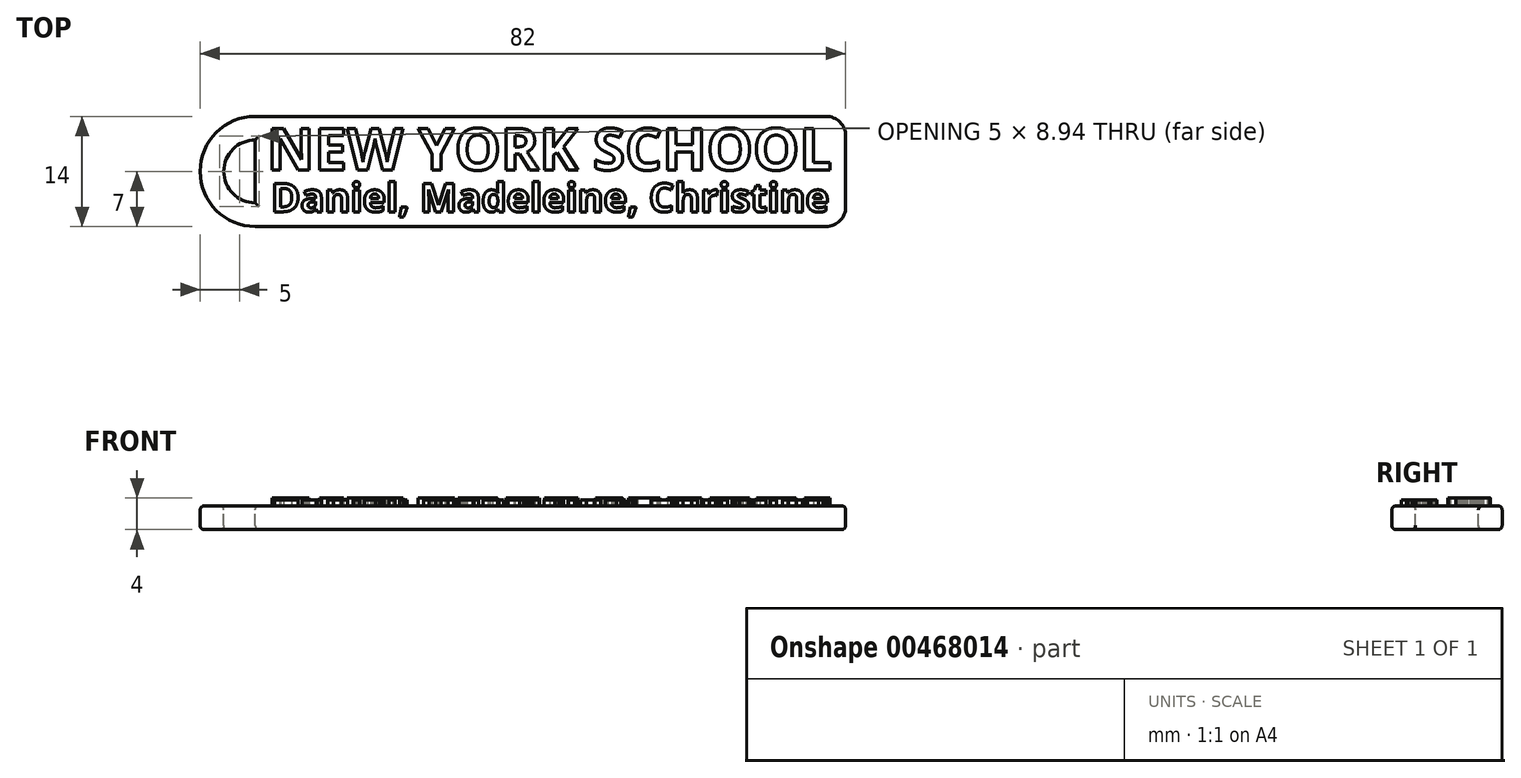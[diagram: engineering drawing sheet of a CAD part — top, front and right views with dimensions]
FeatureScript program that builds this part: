
annotation { "Feature Type Name" : "Feature", "Feature Type Description" : "" }
export const myFeature = defineFeature(function(context is Context, id is Id, definition is map)
    precondition{}
    {
        {
            var Q0;
            Q0=qCreatedBy(makeId("Top.planeOp"),FACE);
            var sketch = newSketch(context, id + "F0", { "sketchPlane" : qUnion([Q0])});
            skLineSegment(sketch, "E0.bottom", {"start": v(37.5, -7) * mm, "end": v(-37.5, -7) * mm});
            skLineSegment(sketch, "E0.top", {"start": v(37.5, 7) * mm, "end": v(-37.5, 7) * mm});
            skLineSegment(sketch, "E0.left", {"start": v(37.5, -7) * mm, "end": v(37.5, 7) * mm});
            skLineSegment(sketch, "E0.right", {"start": v(-37.5, -7) * mm, "end": v(-37.5, 7) * mm});
            skPoint(sketch, "E0.middle", {"position": v(0, 0) * mm});
            skSolve(sketch);
        }
        {
            var Q0;
            Q0=makeQuery(id+"F0.imprint","IMPRINT",FACE,{"disambiguationData":[TD([[makeQuery(id+"F0.imprint","IMPRINT",EDGE,{"derivedFrom":sQuery(id+"F0.wireOp",EDGE,"E0.bottom")}),-1.0]])]});
            extrude(context, id + "F1", {"entities" : qUnion([Q0]), "depth" : 3 * mm, "offsetDistance" : 25 * mm});
        }
        {
            var Q0;
            Q0=makeQuery(id+"F1.opExtrude","CAP_FACE",FACE,{"disambiguationData":[OSD([sQuery(id+"F0.wireOp",EDGE,"E0.bottom"),sQuery(id+"F0.wireOp",EDGE,"E0.top"),sQuery(id+"F0.wireOp",EDGE,"E0.left"),sQuery(id+"F0.wireOp",EDGE,"E0.right")])],"isStart":false});
            var sketch = newSketch(context, id + "F2", { "sketchPlane" : qUnion([Q0])});
            skText(sketch, "E1", { "text": "NEW YORK SCHOOL", "fontName": "OpenSans-Bold.ttf"});
            const initialGuessF2  = {"E1": [-0.036, 0.00018, 1, 0, 0.00532]};
            skSetInitialGuess(sketch, initialGuessF2);
            skSolve(sketch);
        }
        {
            var Q0;
            Q0=makeQuery(id+"F2.imprint","IMPRINT",FACE,{"disambiguationData":[TD([[makeQuery(id+"F2.imprint","IMPRINT",EDGE,{"derivedFrom":sQuery(id+"F2.wireOp",EDGE,"E1.sketch_text.stroke-0")}),-1.0]])]});
            var Q1;
            Q1=makeQuery(id+"F2.imprint","IMPRINT",FACE,{"disambiguationData":[TD([[makeQuery(id+"F2.imprint","IMPRINT",EDGE,{"derivedFrom":sQuery(id+"F2.wireOp",EDGE,"E1.sketch_text.stroke-14")}),-1.0]])]});
            var Q2;
            Q2=makeQuery(id+"F2.imprint","IMPRINT",FACE,{"disambiguationData":[TD([[makeQuery(id+"F2.imprint","IMPRINT",EDGE,{"derivedFrom":sQuery(id+"F2.wireOp",EDGE,"E1.sketch_text.stroke-26")}),-1.0]])]});
            var Q3;
            Q3=makeQuery(id+"F2.imprint","IMPRINT",FACE,{"disambiguationData":[TD([[makeQuery(id+"F2.imprint","IMPRINT",EDGE,{"derivedFrom":sQuery(id+"F2.wireOp",EDGE,"E1.sketch_text.stroke-50")}),-1.0]])]});
            var Q4;
            Q4=makeQuery(id+"F2.imprint","IMPRINT",FACE,{"disambiguationData":[TD([[makeQuery(id+"F2.imprint","IMPRINT",EDGE,{"derivedFrom":sQuery(id+"F2.wireOp",EDGE,"E1.sketch_text.stroke-59")}),-1.0]])]});
            var Q5;
            Q5=makeQuery(id+"F2.imprint","IMPRINT",FACE,{"disambiguationData":[TD([[makeQuery(id+"F2.imprint","IMPRINT",EDGE,{"derivedFrom":sQuery(id+"F2.wireOp",EDGE,"E1.sketch_text.stroke-73")}),-1.0]])]});
            var Q6;
            Q6=makeQuery(id+"F2.imprint","IMPRINT",FACE,{"disambiguationData":[TD([[makeQuery(id+"F2.imprint","IMPRINT",EDGE,{"derivedFrom":sQuery(id+"F2.wireOp",EDGE,"E1.sketch_text.stroke-92")}),-1.0]])]});
            var Q7;
            Q7=makeQuery(id+"F2.imprint","IMPRINT",FACE,{"disambiguationData":[TD([[makeQuery(id+"F2.imprint","IMPRINT",EDGE,{"derivedFrom":sQuery(id+"F2.wireOp",EDGE,"E1.sketch_text.stroke-105")}),-1.0]])]});
            var Q8;
            Q8=makeQuery(id+"F2.imprint","IMPRINT",FACE,{"disambiguationData":[TD([[makeQuery(id+"F2.imprint","IMPRINT",EDGE,{"derivedFrom":sQuery(id+"F2.wireOp",EDGE,"E1.sketch_text.stroke-133")}),-1.0]])]});
            var Q9;
            Q9=makeQuery(id+"F2.imprint","IMPRINT",FACE,{"disambiguationData":[TD([[makeQuery(id+"F2.imprint","IMPRINT",EDGE,{"derivedFrom":sQuery(id+"F2.wireOp",EDGE,"E1.sketch_text.stroke-148")}),-1.0]])]});
            var Q10;
            Q10=makeQuery(id+"F2.imprint","IMPRINT",FACE,{"disambiguationData":[TD([[makeQuery(id+"F2.imprint","IMPRINT",EDGE,{"derivedFrom":sQuery(id+"F2.wireOp",EDGE,"E1.sketch_text.stroke-160")}),-1.0]])]});
            var Q11;
            Q11=makeQuery(id+"F2.imprint","IMPRINT",FACE,{"disambiguationData":[TD([[makeQuery(id+"F2.imprint","IMPRINT",EDGE,{"derivedFrom":sQuery(id+"F2.wireOp",EDGE,"E1.sketch_text.stroke-174")}),-1.0]])]});
            var Q12;
            Q12=makeQuery(id+"F2.imprint","IMPRINT",FACE,{"disambiguationData":[TD([[makeQuery(id+"F2.imprint","IMPRINT",EDGE,{"derivedFrom":sQuery(id+"F2.wireOp",EDGE,"E1.sketch_text.stroke-188")}),-1.0]])]});
            extrude(context, id + "F3", {"entities" : qUnion([Q0, Q1, Q2, Q3, Q4, Q5, Q6, Q7, Q8, Q9, Q10, Q11, Q12]), "operationType" : NewBodyOperationType.ADD, "depth" : 1 * mm, "offsetDistance" : 25 * mm});
        }
        {
            var Q0;
            {var subQ0=sQuery(id+"F0.wireOp",EDGE,"E0.top");var subQ1=sQuery(id+"F0.wireOp",EDGE,"E0.right");var subQ2=sQuery(id+"F0.wireOp",EDGE,"E0.bottom");var subQ3=sQuery(id+"F0.wireOp",EDGE,"E0.left");Q0=makeQuery(id+"F3.boolean.opBoolean","SPLIT",FACE,{"disambiguationData":[TD([makeQuery(id+"F1.opExtrude","SWEPT_FACE",FACE,{"disambiguationData":[OSD([subQ2])]})])],"derivedFrom":makeQuery(id+"F1.opExtrude","CAP_FACE",FACE,{"disambiguationData":[OSD([subQ2,subQ0,subQ3,subQ1])],"isStart":false})});}
            var sketch = newSketch(context, id + "F4", { "sketchPlane" : qUnion([Q0])});
            skText(sketch, "E2", { "text": "Daniel, Madeleine, Christine", "fontName": "OpenSans-Bold.ttf"});
            const initialGuessF4  = {"E2": [-0.0355, -0.00513, 1, 0, 0.00363]};
            skSetInitialGuess(sketch, initialGuessF4);
            skSolve(sketch);
        }
        {
            var Q0;
            Q0=makeQuery(id+"F4.imprint","IMPRINT",FACE,{"disambiguationData":[TD([[makeQuery(id+"F4.imprint","IMPRINT",EDGE,{"derivedFrom":sQuery(id+"F4.wireOp",EDGE,"E2.sketch_text.stroke-0")}),-1.0]])]});
            var Q1;
            Q1=makeQuery(id+"F4.imprint","IMPRINT",FACE,{"disambiguationData":[TD([[makeQuery(id+"F4.imprint","IMPRINT",EDGE,{"derivedFrom":sQuery(id+"F4.wireOp",EDGE,"E2.sketch_text.stroke-14")}),-1.0]])]});
            var Q2;
            Q2=makeQuery(id+"F4.imprint","IMPRINT",FACE,{"disambiguationData":[TD([[makeQuery(id+"F4.imprint","IMPRINT",EDGE,{"derivedFrom":sQuery(id+"F4.wireOp",EDGE,"E2.sketch_text.stroke-41")}),-1.0]])]});
            var Q3;
            Q3=makeQuery(id+"F4.imprint","IMPRINT",FACE,{"disambiguationData":[TD([[makeQuery(id+"F4.imprint","IMPRINT",EDGE,{"derivedFrom":sQuery(id+"F4.wireOp",EDGE,"E2.sketch_text.stroke-62")}),-1.0]])]});
            var Q4;
            Q4=makeQuery(id+"F4.imprint","IMPRINT",FACE,{"disambiguationData":[TD([[makeQuery(id+"F4.imprint","IMPRINT",EDGE,{"derivedFrom":sQuery(id+"F4.wireOp",EDGE,"E2.sketch_text.stroke-58")}),-1.0]])]});
            var Q5;
            Q5=makeQuery(id+"F4.imprint","IMPRINT",FACE,{"disambiguationData":[TD([[makeQuery(id+"F4.imprint","IMPRINT",EDGE,{"derivedFrom":sQuery(id+"F4.wireOp",EDGE,"E2.sketch_text.stroke-70")}),-1.0]])]});
            var Q6;
            Q6=makeQuery(id+"F4.imprint","IMPRINT",FACE,{"disambiguationData":[TD([[makeQuery(id+"F4.imprint","IMPRINT",EDGE,{"derivedFrom":sQuery(id+"F4.wireOp",EDGE,"E2.sketch_text.stroke-89")}),-1.0]])]});
            var Q7;
            Q7=makeQuery(id+"F4.imprint","IMPRINT",FACE,{"disambiguationData":[TD([[makeQuery(id+"F4.imprint","IMPRINT",EDGE,{"derivedFrom":sQuery(id+"F4.wireOp",EDGE,"E2.sketch_text.stroke-93")}),-1.0]])]});
            var Q8;
            Q8=makeQuery(id+"F4.imprint","IMPRINT",FACE,{"disambiguationData":[TD([[makeQuery(id+"F4.imprint","IMPRINT",EDGE,{"derivedFrom":sQuery(id+"F4.wireOp",EDGE,"E2.sketch_text.stroke-100")}),-1.0]])]});
            var Q9;
            Q9=makeQuery(id+"F4.imprint","IMPRINT",FACE,{"disambiguationData":[TD([[makeQuery(id+"F4.imprint","IMPRINT",EDGE,{"derivedFrom":sQuery(id+"F4.wireOp",EDGE,"E2.sketch_text.stroke-118")}),-1.0]])]});
            var Q10;
            Q10=makeQuery(id+"F4.imprint","IMPRINT",FACE,{"disambiguationData":[TD([[makeQuery(id+"F4.imprint","IMPRINT",EDGE,{"derivedFrom":sQuery(id+"F4.wireOp",EDGE,"E2.sketch_text.stroke-145")}),-1.0]])]});
            var Q11;
            Q11=makeQuery(id+"F4.imprint","IMPRINT",FACE,{"disambiguationData":[TD([[makeQuery(id+"F4.imprint","IMPRINT",EDGE,{"derivedFrom":sQuery(id+"F4.wireOp",EDGE,"E2.sketch_text.stroke-169")}),-1.0]])]});
            var Q12;
            Q12=makeQuery(id+"F4.imprint","IMPRINT",FACE,{"disambiguationData":[TD([[makeQuery(id+"F4.imprint","IMPRINT",EDGE,{"derivedFrom":sQuery(id+"F4.wireOp",EDGE,"E2.sketch_text.stroke-188")}),-1.0]])]});
            var Q13;
            Q13=makeQuery(id+"F4.imprint","IMPRINT",FACE,{"disambiguationData":[TD([[makeQuery(id+"F4.imprint","IMPRINT",EDGE,{"derivedFrom":sQuery(id+"F4.wireOp",EDGE,"E2.sketch_text.stroke-192")}),-1.0]])]});
            var Q14;
            Q14=makeQuery(id+"F4.imprint","IMPRINT",FACE,{"disambiguationData":[TD([[makeQuery(id+"F4.imprint","IMPRINT",EDGE,{"derivedFrom":sQuery(id+"F4.wireOp",EDGE,"E2.sketch_text.stroke-211")}),-1.0]])]});
            var Q15;
            Q15=makeQuery(id+"F4.imprint","IMPRINT",FACE,{"disambiguationData":[TD([[makeQuery(id+"F4.imprint","IMPRINT",EDGE,{"derivedFrom":sQuery(id+"F4.wireOp",EDGE,"E2.sketch_text.stroke-215")}),-1.0]])]});
            var Q16;
            Q16=makeQuery(id+"F4.imprint","IMPRINT",FACE,{"disambiguationData":[TD([[makeQuery(id+"F4.imprint","IMPRINT",EDGE,{"derivedFrom":sQuery(id+"F4.wireOp",EDGE,"E2.sketch_text.stroke-223")}),-1.0]])]});
            var Q17;
            Q17=makeQuery(id+"F4.imprint","IMPRINT",FACE,{"disambiguationData":[TD([[makeQuery(id+"F4.imprint","IMPRINT",EDGE,{"derivedFrom":sQuery(id+"F4.wireOp",EDGE,"E2.sketch_text.stroke-240")}),-1.0]])]});
            var Q18;
            Q18=makeQuery(id+"F4.imprint","IMPRINT",FACE,{"disambiguationData":[TD([[makeQuery(id+"F4.imprint","IMPRINT",EDGE,{"derivedFrom":sQuery(id+"F4.wireOp",EDGE,"E2.sketch_text.stroke-259")}),-1.0]])]});
            var Q19;
            Q19=makeQuery(id+"F4.imprint","IMPRINT",FACE,{"disambiguationData":[TD([[makeQuery(id+"F4.imprint","IMPRINT",EDGE,{"derivedFrom":sQuery(id+"F4.wireOp",EDGE,"E2.sketch_text.stroke-266")}),-1.0]])]});
            var Q20;
            Q20=makeQuery(id+"F4.imprint","IMPRINT",FACE,{"disambiguationData":[TD([[makeQuery(id+"F4.imprint","IMPRINT",EDGE,{"derivedFrom":sQuery(id+"F4.wireOp",EDGE,"E2.sketch_text.stroke-281")}),-1.0]])]});
            var Q21;
            Q21=makeQuery(id+"F4.imprint","IMPRINT",FACE,{"disambiguationData":[TD([[makeQuery(id+"F4.imprint","IMPRINT",EDGE,{"derivedFrom":sQuery(id+"F4.wireOp",EDGE,"E2.sketch_text.stroke-299")}),-1.0]])]});
            var Q22;
            Q22=makeQuery(id+"F4.imprint","IMPRINT",FACE,{"disambiguationData":[TD([[makeQuery(id+"F4.imprint","IMPRINT",EDGE,{"derivedFrom":sQuery(id+"F4.wireOp",EDGE,"E2.sketch_text.stroke-312")}),-1.0]])]});
            var Q23;
            Q23=makeQuery(id+"F4.imprint","IMPRINT",FACE,{"disambiguationData":[TD([[makeQuery(id+"F4.imprint","IMPRINT",EDGE,{"derivedFrom":sQuery(id+"F4.wireOp",EDGE,"E2.sketch_text.stroke-316")}),-1.0]])]});
            var Q24;
            Q24=makeQuery(id+"F4.imprint","IMPRINT",FACE,{"disambiguationData":[TD([[makeQuery(id+"F4.imprint","IMPRINT",EDGE,{"derivedFrom":sQuery(id+"F4.wireOp",EDGE,"E2.sketch_text.stroke-324")}),-1.0]])]});
            var Q25;
            Q25=makeQuery(id+"F4.imprint","IMPRINT",FACE,{"disambiguationData":[TD([[makeQuery(id+"F4.imprint","IMPRINT",EDGE,{"derivedFrom":sQuery(id+"F4.wireOp",EDGE,"E2.sketch_text.stroke-349")}),-1.0]])]});
            var Q26;
            Q26=makeQuery(id+"F4.imprint","IMPRINT",FACE,{"disambiguationData":[TD([[makeQuery(id+"F4.imprint","IMPRINT",EDGE,{"derivedFrom":sQuery(id+"F4.wireOp",EDGE,"E2.sketch_text.stroke-372")}),-1.0]])]});
            var Q27;
            Q27=makeQuery(id+"F4.imprint","IMPRINT",FACE,{"disambiguationData":[TD([[makeQuery(id+"F4.imprint","IMPRINT",EDGE,{"derivedFrom":sQuery(id+"F4.wireOp",EDGE,"E2.sketch_text.stroke-368")}),-1.0]])]});
            var Q28;
            Q28=makeQuery(id+"F4.imprint","IMPRINT",FACE,{"disambiguationData":[TD([[makeQuery(id+"F4.imprint","IMPRINT",EDGE,{"derivedFrom":sQuery(id+"F4.wireOp",EDGE,"E2.sketch_text.stroke-380")}),-1.0]])]});
            var Q29;
            Q29=makeQuery(id+"F4.imprint","IMPRINT",FACE,{"disambiguationData":[TD([[makeQuery(id+"F4.imprint","IMPRINT",EDGE,{"derivedFrom":sQuery(id+"F4.wireOp",EDGE,"E2.sketch_text.stroke-397")}),-1.0]])]});
            var Q30;
            Q30=makeQuery(id+"F4.imprint","IMPRINT",FACE,{"disambiguationData":[TD([[makeQuery(id+"F4.imprint","IMPRINT",EDGE,{"derivedFrom":sQuery(id+"F4.wireOp",EDGE,"E2.sketch_text.stroke-83")}),-1.0]])]});
            var Q31;
            Q31=makeQuery(id+"F4.imprint","IMPRINT",FACE,{"disambiguationData":[TD([[makeQuery(id+"F4.imprint","IMPRINT",EDGE,{"derivedFrom":sQuery(id+"F4.wireOp",EDGE,"E2.sketch_text.stroke-179")}),-1.0]])]});
            var Q32;
            Q32=makeQuery(id+"F4.imprint","IMPRINT",FACE,{"disambiguationData":[TD([[makeQuery(id+"F4.imprint","IMPRINT",EDGE,{"derivedFrom":sQuery(id+"F4.wireOp",EDGE,"E2.sketch_text.stroke-286")}),-1.0]])]});
            var Q33;
            Q33=makeQuery(id+"F4.imprint","IMPRINT",FACE,{"disambiguationData":[TD([[makeQuery(id+"F4.imprint","IMPRINT",EDGE,{"derivedFrom":sQuery(id+"F4.wireOp",EDGE,"E2.sketch_text.stroke-249")}),-1.0]])]});
            var Q34;
            Q34=makeQuery(id+"F4.imprint","IMPRINT",FACE,{"disambiguationData":[TD([[makeQuery(id+"F4.imprint","IMPRINT",EDGE,{"derivedFrom":sQuery(id+"F4.wireOp",EDGE,"E2.sketch_text.stroke-304")}),-1.0]])]});
            var Q35;
            Q35=makeQuery(id+"F4.imprint","IMPRINT",FACE,{"disambiguationData":[TD([[makeQuery(id+"F4.imprint","IMPRINT",EDGE,{"derivedFrom":sQuery(id+"F4.wireOp",EDGE,"E2.sketch_text.stroke-357")}),-1.0]])]});
            var Q36;
            Q36=makeQuery(id+"F4.imprint","IMPRINT",FACE,{"disambiguationData":[TD([[makeQuery(id+"F4.imprint","IMPRINT",EDGE,{"derivedFrom":sQuery(id+"F4.wireOp",EDGE,"E2.sketch_text.stroke-352")}),-1.0]])]});
            var Q37;
            Q37=makeQuery(id+"F4.imprint","IMPRINT",FACE,{"disambiguationData":[TD([[makeQuery(id+"F4.imprint","IMPRINT",EDGE,{"derivedFrom":sQuery(id+"F4.wireOp",EDGE,"E2.sketch_text.stroke-203")}),-1.0]])]});
            extrude(context, id + "F5", {"entities" : qUnion([Q0, Q1, Q2, Q3, Q4, Q5, Q6, Q7, Q8, Q9, Q10, Q11, Q12, Q13, Q14, Q15, Q16, Q17, Q18, Q19, Q20, Q21, Q22, Q23, Q24, Q25, Q26, Q27, Q28, Q29, Q30, Q31, Q32, Q33, Q34, Q35, Q36, Q37]), "operationType" : NewBodyOperationType.ADD, "depth" : 0.75 * mm, "offsetDistance" : 25 * mm});
        }
        {
            var Q0;
            {var subQ0=sQuery(id+"F0.wireOp",EDGE,"E0.top");var subQ105=sQuery(id+"F0.wireOp",EDGE,"E0.right");var subQ117=sQuery(id+"F0.wireOp",EDGE,"E0.left");var subQ175=sQuery(id+"F0.wireOp",EDGE,"E0.bottom");var subQ176=makeQuery(id+"F1.opExtrude","SWEPT_FACE",FACE,{"disambiguationData":[OSD([subQ175])]});Q0=makeQuery(id+"F5.boolean.opBoolean","SPLIT",FACE,{"disambiguationData":[TD([subQ176])],"derivedFrom":makeQuery(id+"F3.boolean.opBoolean","SPLIT",FACE,{"disambiguationData":[TD([subQ176])],"derivedFrom":makeQuery(id+"F1.opExtrude","CAP_FACE",FACE,{"disambiguationData":[OSD([subQ175,subQ0,subQ117,subQ105])],"isStart":false})})});}
            var sketch = newSketch(context, id + "F6", { "sketchPlane" : qUnion([Q0])});
            skArc(sketch, "E3", {"start": v(-37.5, 7) * mm, "mid": v(-44.5, 0) * mm, "end": v(-37.5, -7) * mm});
            skArc(sketch, "E4", {"start": v(-37.5, -4) * mm, "mid": v(-41.5, 0) * mm, "end": v(-37.5, 4) * mm});
            skSolve(sketch);
        }
        {
            var Q0;
            {var subQ0=sQuery(id+"F6.wireOp",EDGE,"E3");Q0=makeQuery(id+"F6.imprint","IMPRINT",FACE,{"disambiguationData":[TD([[makeQuery(id+"F6.imprint","IMPRINT",EDGE,{"derivedFrom":subQ0}),1.0]])]});}
            extrude(context, id + "F7", {"entities" : qUnion([Q0]), "operationType" : NewBodyOperationType.ADD, "oppositeDirection" : true, "depth" : 3 * mm, "offsetDistance" : 25 * mm});
        }
        {
            var Q0;
            Q0=makeQuery(id+"F1.opExtrude","SWEPT_EDGE",EDGE,{"disambiguationData":[OSD([sQuery(id+"F0.wireOp",EDGE,"E0.top"),sQuery(id+"F0.wireOp",EDGE,"E0.left")])]});
            var Q1;
            Q1=makeQuery(id+"F1.opExtrude","SWEPT_EDGE",EDGE,{"disambiguationData":[OSD([sQuery(id+"F0.wireOp",EDGE,"E0.bottom"),sQuery(id+"F0.wireOp",EDGE,"E0.left")])]});
            fillet(context, id + "F8", {"entities" : qUnion([Q0, Q1]), "radius" : 2.5 * mm, "tangentPropagation" : true, "allowEdgeOverflow" : false});
        }
        {
            var Q0;
            Q0=makeQuery(id+"F7.opExtrude","CAP_EDGE",EDGE,{"disambiguationData":[OSD([sQuery(id+"F6.wireOp",EDGE,"E4")])],"isStart":true});
            var Q1;
            Q1=makeQuery(id+"F1.opExtrude","CAP_EDGE",EDGE,{"disambiguationData":[OSD([sQuery(id+"F0.wireOp",EDGE,"E0.right")])],"isStart":false});
            var Q2;
            Q2=makeQuery(id+"F1.opExtrude","CAP_EDGE",EDGE,{"disambiguationData":[OSD([sQuery(id+"F0.wireOp",EDGE,"E0.top")])],"isStart":false});
            var Q3;
            Q3=makeQuery(id+"F7.opExtrude","CAP_EDGE",EDGE,{"disambiguationData":[OSD([sQuery(id+"F6.wireOp",EDGE,"E4")])],"isStart":false});
            var Q4;
            Q4=makeQuery(id+"F7.opExtrude","CAP_EDGE",EDGE,{"disambiguationData":[OSD([sQuery(id+"F6.wireOp",EDGE,"E3")])],"isStart":false});
            var Q5;
            Q5=makeQuery(id+"F1.opExtrude","CAP_EDGE",EDGE,{"disambiguationData":[OSD([sQuery(id+"F0.wireOp",EDGE,"E0.right")])],"isStart":true});
            fillet(context, id + "F9", {"entities" : qUnion([Q0, Q1, Q2, Q3, Q4, Q5]), "radius" : 0.5 * mm, "tangentPropagation" : true, "allowEdgeOverflow" : false});
        }
    });
